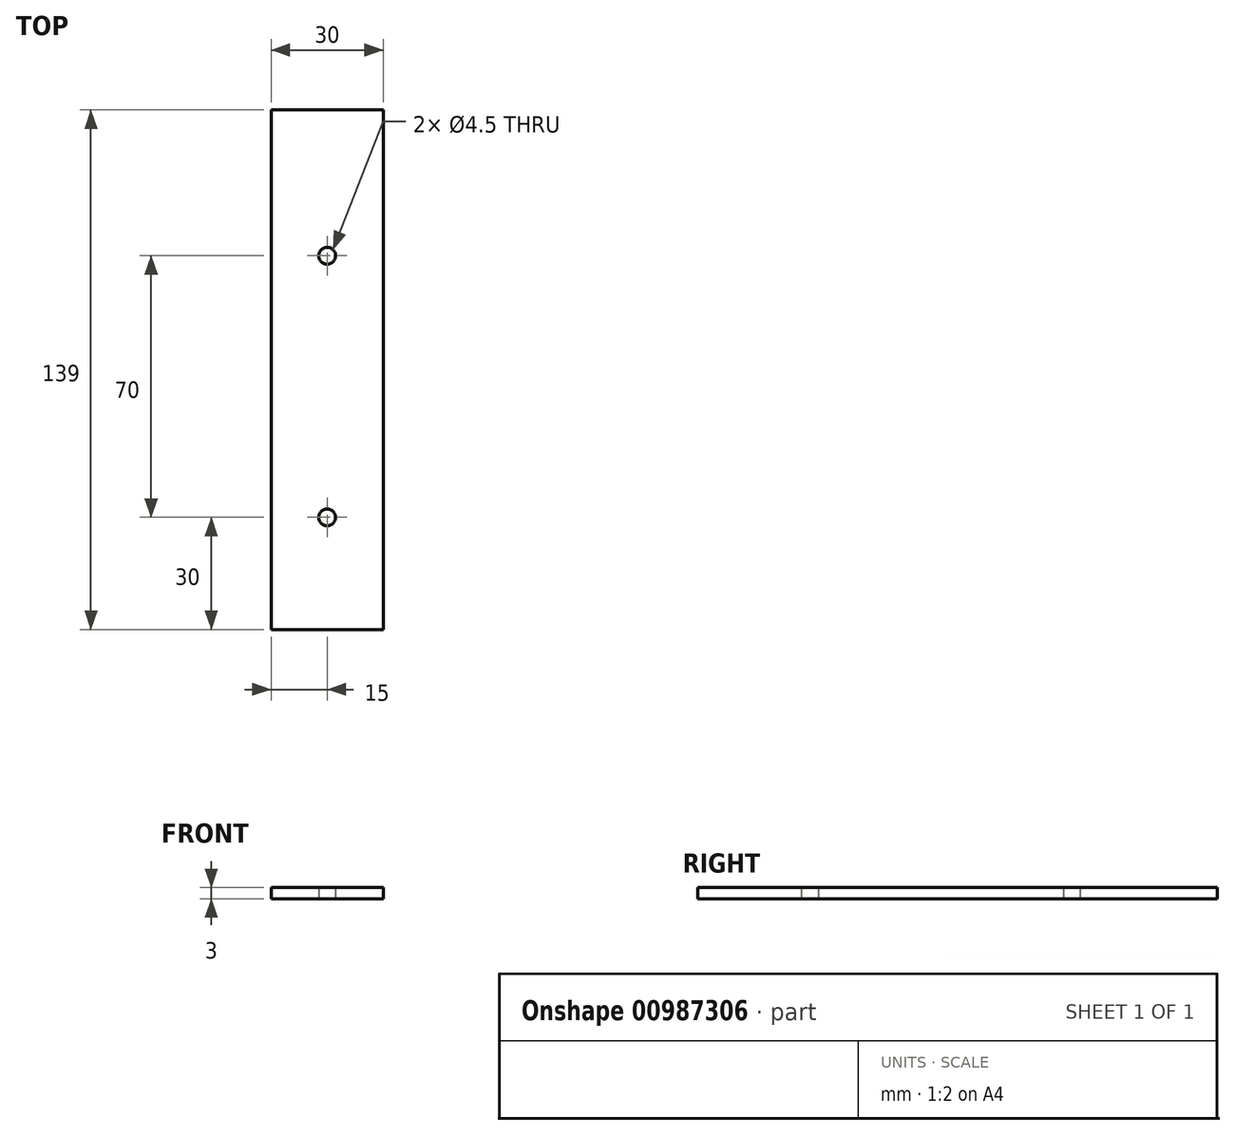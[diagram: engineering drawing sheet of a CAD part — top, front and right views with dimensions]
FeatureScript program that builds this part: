
annotation { "Feature Type Name" : "Feature", "Feature Type Description" : "" }
export const myFeature = defineFeature(function(context is Context, id is Id, definition is map)
    precondition{}
    {
        {
            var Q0;
            Q0=qCreatedBy(makeId("Top.planeOp"),FACE);
            var sketch = newSketch(context, id + "F0", { "sketchPlane" : qUnion([Q0])});
            skLineSegment(sketch, "E0.bottom", {"start": v(0, 0) * mm, "end": v(30, 0) * mm});
            skLineSegment(sketch, "E0.top", {"start": v(0, 139) * mm, "end": v(30, 139) * mm});
            skLineSegment(sketch, "E0.left", {"start": v(0, 0) * mm, "end": v(0, 139) * mm});
            skLineSegment(sketch, "E0.right", {"start": v(30, 0) * mm, "end": v(30, 139) * mm});
            skCircle(sketch, "E1", {"center": v(15, 30) * mm, "radius": 2.25 * mm});
            skCircle(sketch, "E2", {"center": v(15, 100) * mm, "radius": 2.25 * mm});
            skSolve(sketch);
        }
        {
            var Q0;
            Q0=makeQuery(id+"F0.imprint","IMPRINT",FACE,{"disambiguationData":[TD([[makeQuery(id+"F0.imprint","IMPRINT",EDGE,{"derivedFrom":sQuery(id+"F0.wireOp",EDGE,"E0.bottom")}),1.0]])]});
            extrude(context, id + "F1", {"entities" : qUnion([Q0]), "depth" : 3 * mm, "offsetDistance" : 25 * mm});
        }
    });
